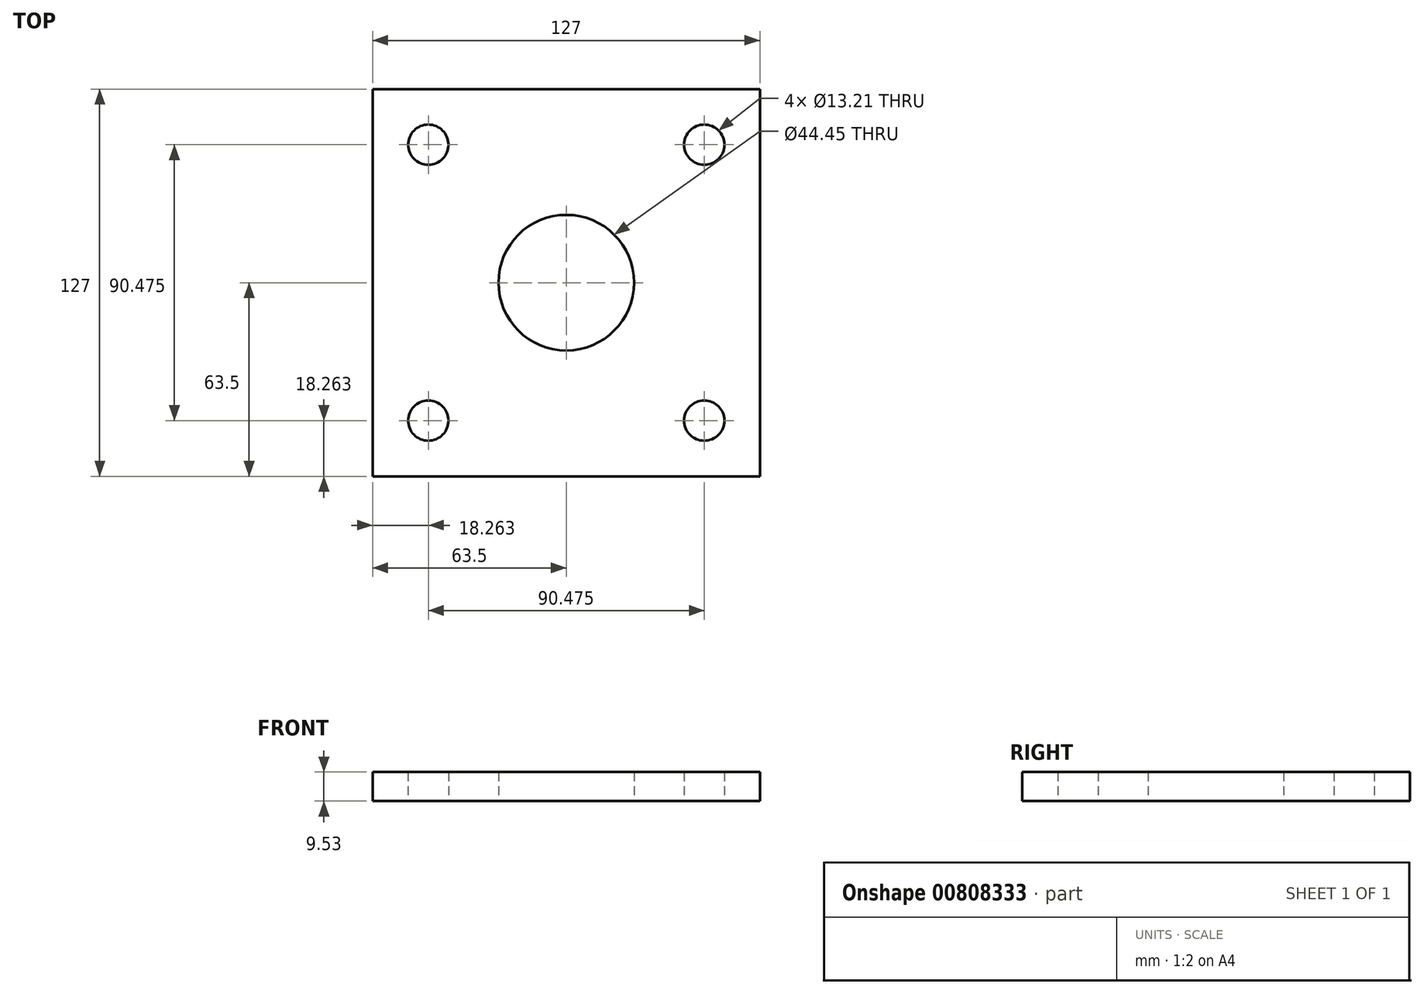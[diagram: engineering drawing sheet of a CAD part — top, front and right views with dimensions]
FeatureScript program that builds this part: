
annotation { "Feature Type Name" : "Feature", "Feature Type Description" : "" }
export const myFeature = defineFeature(function(context is Context, id is Id, definition is map)
    precondition{}
    {
        {
            var Q0;
            Q0=qCreatedBy(makeId("Top.planeOp"),FACE);
            var sketch = newSketch(context, id + "F0", { "sketchPlane" : qUnion([Q0])});
            skLineSegment(sketch, "E0.bottom", {"start": v(63.5, -63.5) * mm, "end": v(-63.5, -63.5) * mm});
            skLineSegment(sketch, "E0.top", {"start": v(63.5, 63.5) * mm, "end": v(-63.5, 63.5) * mm});
            skLineSegment(sketch, "E0.left", {"start": v(63.5, -63.5) * mm, "end": v(63.5, 63.5) * mm});
            skLineSegment(sketch, "E0.right", {"start": v(-63.5, -63.5) * mm, "end": v(-63.5, 63.5) * mm});
            skCircle(sketch, "E1", {"center": v(0, 0) * mm, "radius": 22.23 * mm});
            skCircle(sketch, "E2", {"center": v(-45.24, 45.24) * mm, "radius": 6.6 * mm});
            skCircle(sketch, "E3", {"center": v(45.24, 45.24) * mm, "radius": 6.6 * mm});
            skCircle(sketch, "E4", {"center": v(-45.24, -45.24) * mm, "radius": 6.6 * mm});
            skCircle(sketch, "E5", {"center": v(45.24, -45.24) * mm, "radius": 6.6 * mm});
            skSolve(sketch);
        }
        {
            var Q0;
            Q0=makeQuery(id+"F0.imprint","IMPRINT",FACE,{"disambiguationData":[TD([[makeQuery(id+"F0.imprint","IMPRINT",EDGE,{"derivedFrom":sQuery(id+"F0.wireOp",EDGE,"E0.bottom")}),-1.0]])]});
            extrude(context, id + "F1", {"entities" : qUnion([Q0]), "depth" : 9.52 * mm, "offsetDistance" : 25.4 * mm});
        }
    });
